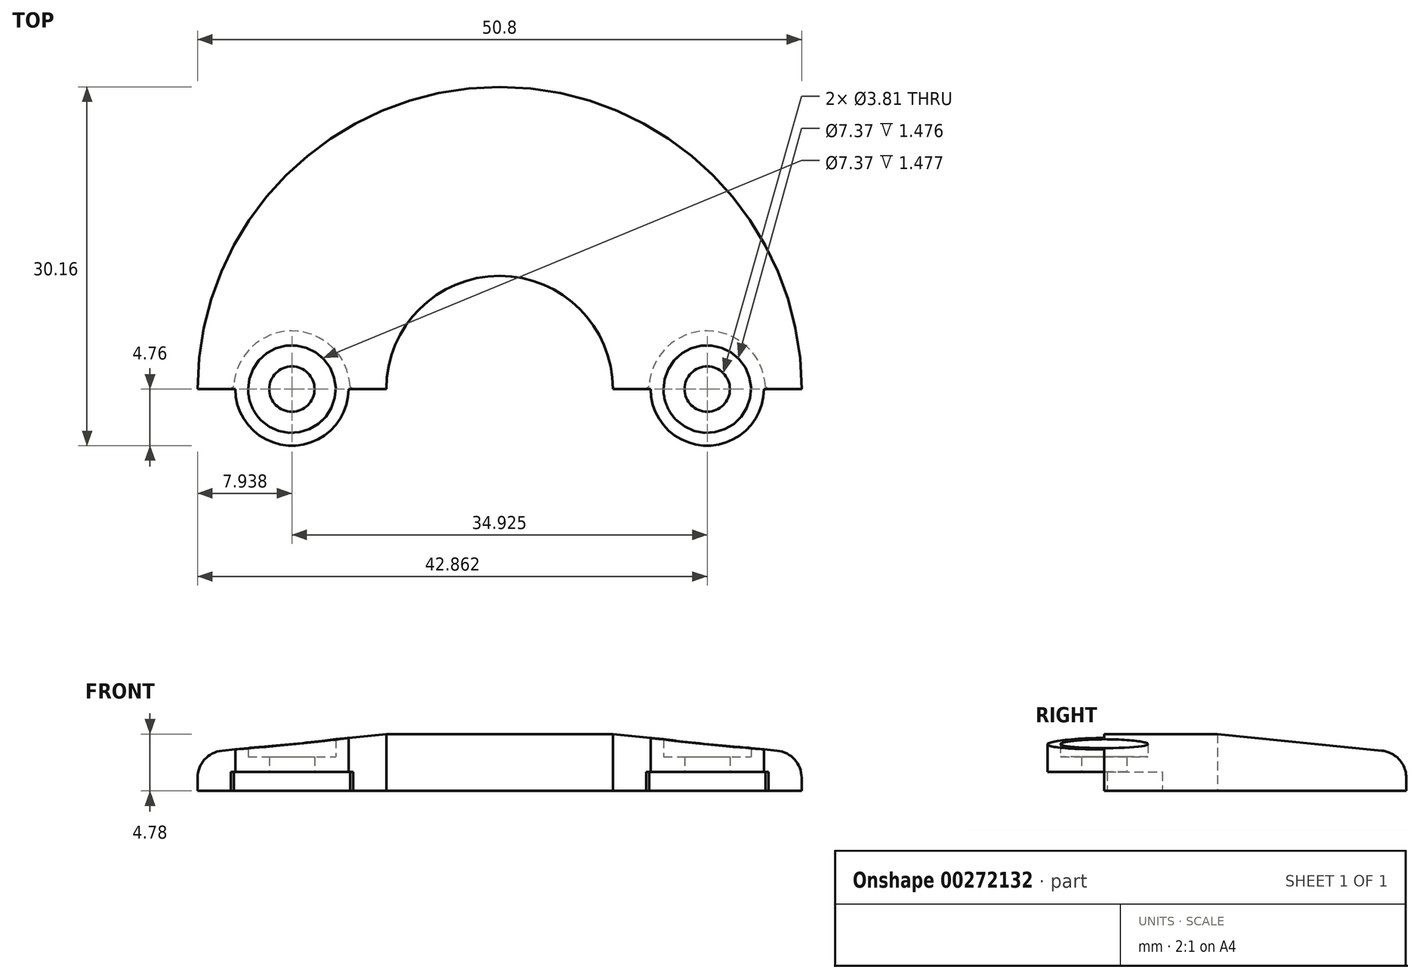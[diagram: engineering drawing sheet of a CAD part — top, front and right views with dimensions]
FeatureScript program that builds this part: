
annotation { "Feature Type Name" : "Feature", "Feature Type Description" : "" }
export const myFeature = defineFeature(function(context is Context, id is Id, definition is map)
    precondition{}
    {
        {
            var Q0;
            Q0=qCreatedBy(makeId("Front.planeOp"),FACE);
            var sketch = newSketch(context, id + "F0", { "sketchPlane" : qUnion([Q0])});
            skLineSegment(sketch, "E0", {"start": v(9.53, 0) * mm, "end": v(25.4, 0) * mm});
            skLineSegment(sketch, "E1", {"start": v(25.4, 0) * mm, "end": v(25.4, 1.1) * mm});
            skLineSegment(sketch, "E2", {"start": v(23.34, 3.38) * mm, "end": v(9.52, 4.78) * mm});
            skLineSegment(sketch, "E3", {"start": v(9.53, 4.78) * mm, "end": v(9.53, 0) * mm});
            skPoint(sketch, "E4.visualSharp", {"position": v(25.4, 3.18) * mm});
            skArc(sketch, "E4.filletArc", {"start": v(25.4, 1.1) * mm, "mid": v(24.8, 2.64) * mm, "end": v(23.34, 3.38) * mm});
            skLineSegment(sketch, "E5", {"start": v(0, 0) * mm, "end": v(0, 4.4) * mm});
            skSolve(sketch);
        }
        {
            var Q0;
            Q0=makeQuery(id+"F0.imprint","IMPRINT",FACE,{"disambiguationData":[TD([[makeQuery(id+"F0.imprint","IMPRINT",EDGE,{"derivedFrom":sQuery(id+"F0.wireOp",EDGE,"E0")}),1.0]])]});
            var Q1;
            Q1=sQuery(id+"F0.wireOp",EDGE,"E5");
            revolve(context, id + "F1", {"entities" : qUnion([Q0]), "axis" : qUnion([Q1]), "revolveType" : RevolveType.FULL});
        }
        {
            var Q0;
            Q0=makeQuery(id+"F1.opRevolve","SWEPT_FACE",FACE,{"disambiguationData":[OSD([sQuery(id+"F0.wireOp",EDGE,"E0")])]});
            var sketch = newSketch(context, id + "F2", { "sketchPlane" : qUnion([Q0])});
            skLineSegment(sketch, "E6.bottom", {"start": v(-25.4, 0) * mm, "end": v(-22.23, 0) * mm});
            skLineSegment(sketch, "E6.top", {"start": v(-25.4, 25.4) * mm, "end": v(25.4, 25.4) * mm});
            skLineSegment(sketch, "E6.left", {"start": v(-25.4, 0) * mm, "end": v(-25.4, 25.4) * mm});
            skLineSegment(sketch, "E6.right", {"start": v(25.4, 0) * mm, "end": v(25.4, 25.4) * mm});
            skArc(sketch, "E7", {"start": v(-12.7, 0) * mm, "mid": v(-17.46, 4.76) * mm, "end": v(-22.23, 0) * mm});
            skArc(sketch, "E8", {"start": v(22.22, 0) * mm, "mid": v(17.46, 4.76) * mm, "end": v(12.7, 0) * mm});
            skCircle(sketch, "E9", {"center": v(0, 0) * mm, "radius": 9.53 * mm});
            skLineSegment(sketch, "E10.trimOffspring", {"start": v(9.53, 0) * mm, "end": v(12.7, 0) * mm});
            skLineSegment(sketch, "E11.trimOffspring", {"start": v(-12.7, 0) * mm, "end": v(-9.53, 0) * mm});
            skLineSegment(sketch, "E12.trimOffspring", {"start": v(22.22, 0) * mm, "end": v(25.4, 0) * mm});
            skSolve(sketch);
        }
        {
            var Q0;
            Q0=qSketchRegion(id+"F2",true);
            extrude(context, id + "F3", {"entities" : qUnion([Q0]), "operationType" : NewBodyOperationType.REMOVE, "endBound" : BoundingType.THROUGH_ALL, "oppositeDirection" : true, "depth" : 25.4 * mm});
        }
        {
            var Q0;
            Q0=makeQuery(id+"F1.opRevolve","SWEPT_FACE",FACE,{"disambiguationData":[OSD([sQuery(id+"F0.wireOp",EDGE,"E0")])]});
            var sketch = newSketch(context, id + "F4", { "sketchPlane" : qUnion([Q0])});
            skCircle(sketch, "E13", {"center": v(-17.46, 0) * mm, "radius": 4.89 * mm});
            skCircle(sketch, "E14", {"center": v(17.46, 0) * mm, "radius": 4.89 * mm});
            skSolve(sketch);
        }
        {
            var Q0;
            Q0 = qSketchRegion(id + "F4", true);
            extrude(context, id + "F5", {"entities" : qUnion([Q0]), "operationType" : NewBodyOperationType.REMOVE, "oppositeDirection" : true, "depth" : 1.6 * mm});
        }
        {
            var Q0;
            Q0=makeQuery(id+"F5.boolean.opBoolean","COPY",FACE,{"derivedFrom":makeQuery(id+"F5.opExtrude","CAP_FACE",FACE,{"disambiguationData":[OSD([sQuery(id+"F4.wireOp",EDGE,"E13")])],"isStart":false})});
            var sketch = newSketch(context, id + "F6", { "sketchPlane" : qUnion([Q0])});
            skCircle(sketch, "E15", {"center": v(-17.46, 0) * mm, "radius": 1.9 * mm});
            skCircle(sketch, "E16", {"center": v(17.46, 0) * mm, "radius": 1.9 * mm});
            skSolve(sketch);
        }
        {
            var Q0;
            Q0 = qSketchRegion(id + "F6", true);
            extrude(context, id + "F7", {"entities" : qUnion([Q0]), "operationType" : NewBodyOperationType.REMOVE, "endBound" : BoundingType.THROUGH_ALL, "oppositeDirection" : true, "depth" : 25.4 * mm});
        }
        {
            var Q0;
            Q0=makeQuery(id+"F5.boolean.opBoolean","COPY",FACE,{"derivedFrom":makeQuery(id+"F5.opExtrude","CAP_FACE",FACE,{"disambiguationData":[OSD([sQuery(id+"F4.wireOp",EDGE,"E14")])],"isStart":false})});
            cPlane(context, id + "F8", {"entities" : qUnion([Q0]), "cplaneType" : CPlaneType.OFFSET, "offset" : 1.27 * mm, "oppositeDirection" : true, "width" : 152.4 * mm, "height" : 152.4 * mm});
        }
        {
            var Q0;
            Q0=qCreatedBy(id+"F8.planeOp",FACE);
            var sketch = newSketch(context, id + "F9", { "sketchPlane" : qUnion([Q0])});
            skCircle(sketch, "E17", {"center": v(17.46, 0) * mm, "radius": 3.68 * mm});
            skCircle(sketch, "E18", {"center": v(-17.46, 0) * mm, "radius": 3.68 * mm});
            skSolve(sketch);
        }
        {
            var Q0;
            Q0 = qSketchRegion(id + "F9", true);
            extrude(context, id + "F10", {"entities" : qUnion([Q0]), "operationType" : NewBodyOperationType.REMOVE, "endBound" : BoundingType.THROUGH_ALL, "oppositeDirection" : true, "depth" : 25.4 * mm});
        }
        {
            var Q0;
            Q0=makeQuery(id+"F5.boolean.opBoolean","INTERSECT",EDGE,{"derivedFrom":[makeQuery(id+"F3.boolean.opBoolean","COPY",FACE,{"derivedFrom":makeQuery(id+"F3.opExtrude","SWEPT_FACE",FACE,{"disambiguationData":[OSD([sQuery(id+"F2.wireOp",EDGE,"E6.bottom")])]})}),makeQuery(id+"F5.opExtrude","SWEPT_FACE",FACE,{"disambiguationData":[OSD([sQuery(id+"F4.wireOp",EDGE,"E13")])]})]});
            var Q1;
            Q1=makeQuery(id+"F5.boolean.opBoolean","INTERSECT",EDGE,{"derivedFrom":[makeQuery(id+"F3.boolean.opBoolean","COPY",FACE,{"derivedFrom":makeQuery(id+"F3.opExtrude","SWEPT_FACE",FACE,{"disambiguationData":[OSD([sQuery(id+"F2.wireOp",EDGE,"E11.trimOffspring")])]})}),makeQuery(id+"F5.opExtrude","SWEPT_FACE",FACE,{"disambiguationData":[OSD([sQuery(id+"F4.wireOp",EDGE,"E13")])]})]});
            var Q2;
            Q2=makeQuery(id+"F5.boolean.opBoolean","INTERSECT",EDGE,{"derivedFrom":[makeQuery(id+"F3.boolean.opBoolean","COPY",FACE,{"derivedFrom":makeQuery(id+"F3.opExtrude","SWEPT_FACE",FACE,{"disambiguationData":[OSD([sQuery(id+"F2.wireOp",EDGE,"E10.trimOffspring")])]})}),makeQuery(id+"F5.opExtrude","SWEPT_FACE",FACE,{"disambiguationData":[OSD([sQuery(id+"F4.wireOp",EDGE,"E14")])]})]});
            var Q3;
            Q3=makeQuery(id+"F5.boolean.opBoolean","INTERSECT",EDGE,{"derivedFrom":[makeQuery(id+"F3.boolean.opBoolean","COPY",FACE,{"derivedFrom":makeQuery(id+"F3.opExtrude","SWEPT_FACE",FACE,{"disambiguationData":[OSD([sQuery(id+"F2.wireOp",EDGE,"E12.trimOffspring")])]})}),makeQuery(id+"F5.opExtrude","SWEPT_FACE",FACE,{"disambiguationData":[OSD([sQuery(id+"F4.wireOp",EDGE,"E14")])]})]});
            chamfer(context, id + "F11", {"entities" : qUnion([Q0, Q1, Q2, Q3]), "width" : 0.25 * mm, "tangentPropagation" : true});
        }
    });
